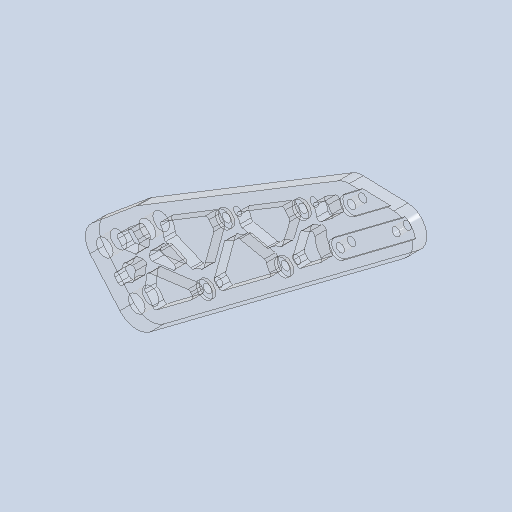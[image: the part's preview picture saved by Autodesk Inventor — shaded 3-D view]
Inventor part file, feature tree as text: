
AUTODESK INVENTOR PART (.ipt)
format: ipt  version: 2023 (Build 270158030, 158C)  size: 803,328 bytes
history: native  units: mm
features: sketch x10, extrude x8, projected_geometry x8, other x3, hole x2, fillet x2
ambient origin geometry x8: Origin, YZ Plane, XZ Plane, XY Plane, X Axis, Y Axis, Z Axis, Center Point
bodies: Body1 (feature_tree)
feature tree (33):
  other  "ソリッド1"
  sketch  "スケッチ1"
  extrude  "押し出し1"  Depth=5.0mm TaperAngle=0.0deg
  extrude  "押し出し2"  Depth=1.0mm TaperAngle=0.0deg
  extrude  "押し出し3"  Depth=6.0mm
  sketch  "スケッチ4"
  hole  "穴2"  [1 undecoded]
  extrude  "押し出し4"  Depth=1.0mm TaperAngle=0.0deg
  hole  "穴3"  [1 undecoded]
  sketch  "スケッチ6"
  extrude  "押し出し6"  Depth=6.0mm
  fillet  "フィレット1"  Radius=6.0mm
  extrude  "押し出し7"  Depth=6.0mm
  fillet  "フィレット2"  Radius=6.0mm
  sketch  "スケッチ9"
  sketch  "スケッチ10"
  extrude  "押し出し8"  Depth=6.0mm
  extrude  "押し出し9"  Depth=104.187773mm
  sketch  "スケッチ2"
  sketch  "スケッチ3"
  projected_geometry  "投影ループ1"
  sketch  "スケッチ5"
  projected_geometry  "投影ループ2"
  sketch  "スケッチ7"
  projected_geometry  "投影ループ3"
  projected_geometry  "投影ループ4"
  projected_geometry  "投影ループ5"
  sketch  "スケッチ8"
  projected_geometry  "投影ループ6"
  projected_geometry  "投影ループ7"
  projected_geometry  "投影ループ8"
  other  "断面エッジを投影1"
  other  "断面エッジを投影2"
note: 2 required parameter values undecoded (feature->parameter linkage not recoverable at this tier; creation-order binding heuristic only, values carry confidence <= 0.55)
